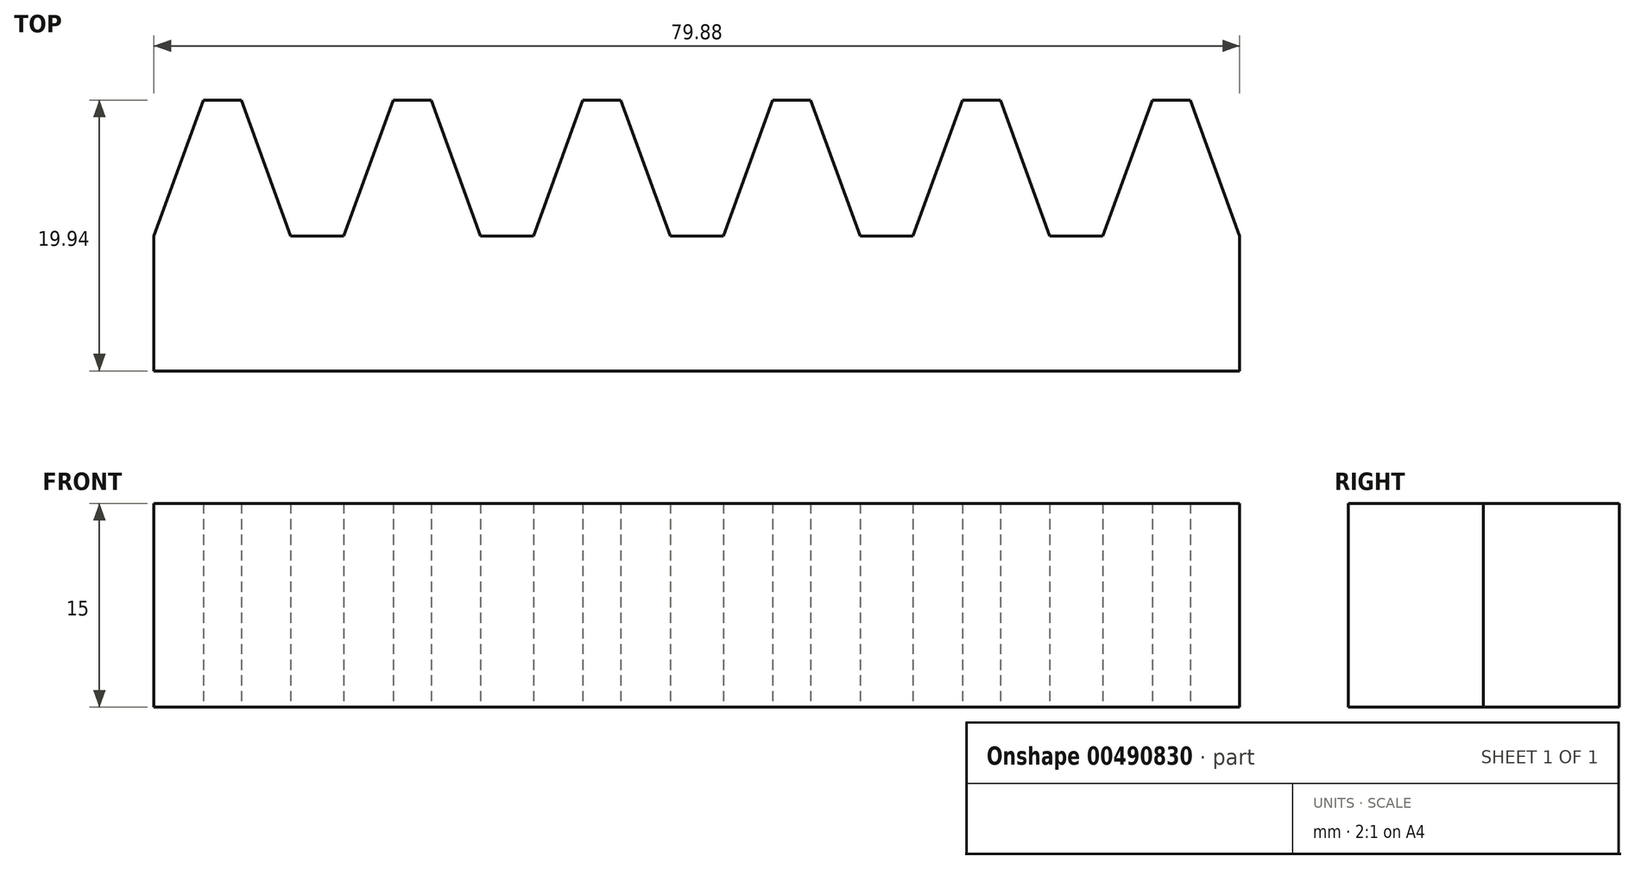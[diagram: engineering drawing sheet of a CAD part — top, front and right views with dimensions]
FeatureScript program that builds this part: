
annotation { "Feature Type Name" : "Feature", "Feature Type Description" : "" }
export const myFeature = defineFeature(function(context is Context, id is Id, definition is map)
    precondition{}
    {
        {
            var Q0;
            Q0=qCreatedBy(makeId("Top.planeOp"),FACE);
            var sketch = newSketch(context, id + "F0", { "sketchPlane" : qUnion([Q0])});
            skPoint(sketch, "E0.middle", {"position": v(1.95, 0.04) * mm});
            skLineSegment(sketch, "E1", {"start": v(1.95, 0.04) * mm, "end": v(5.59, 10.04) * mm});
            skLineSegment(sketch, "E2", {"start": v(5.59, 10.04) * mm, "end": v(8.37, 10.04) * mm});
            skLineSegment(sketch, "E3", {"start": v(8.37, 10.04) * mm, "end": v(12.01, 0.04) * mm});
            skLineSegment(sketch, "E4", {"start": v(12.01, 0.04) * mm, "end": v(15.91, 0.04) * mm});
            skLineSegment(sketch, "E5", {"start": v(15.91, 0.04) * mm, "end": v(19.55, 10.04) * mm});
            skLineSegment(sketch, "E6", {"start": v(19.55, 10.04) * mm, "end": v(22.34, 10.04) * mm});
            skLineSegment(sketch, "E7", {"start": v(22.34, 10.04) * mm, "end": v(25.98, 0.04) * mm});
            skLineSegment(sketch, "E8", {"start": v(25.98, 0.04) * mm, "end": v(29.87, 0.04) * mm});
            skLineSegment(sketch, "E9", {"start": v(29.87, 0.04) * mm, "end": v(33.51, 10.04) * mm});
            skLineSegment(sketch, "E10", {"start": v(33.51, 10.04) * mm, "end": v(36.3, 10.04) * mm});
            skLineSegment(sketch, "E11", {"start": v(36.3, 10.04) * mm, "end": v(39.94, 0.04) * mm});
            skPoint(sketch, "E12.middle", {"position": v(-53.9, 0.04) * mm});
            skLineSegment(sketch, "E13", {"start": v(-39.94, 0.04) * mm, "end": v(-36.3, 10.04) * mm});
            skLineSegment(sketch, "E14", {"start": v(-36.3, 10.04) * mm, "end": v(-33.51, 10.04) * mm});
            skLineSegment(sketch, "E15", {"start": v(-33.51, 10.04) * mm, "end": v(-29.87, 0.04) * mm});
            skLineSegment(sketch, "E16", {"start": v(-29.87, 0.04) * mm, "end": v(-25.97, 0.04) * mm});
            skLineSegment(sketch, "E17", {"start": v(-25.97, 0.04) * mm, "end": v(-22.34, 10.04) * mm});
            skLineSegment(sketch, "E18", {"start": v(-22.34, 10.04) * mm, "end": v(-19.55, 10.04) * mm});
            skLineSegment(sketch, "E19", {"start": v(-19.55, 10.04) * mm, "end": v(-15.91, 0.04) * mm});
            skLineSegment(sketch, "E20", {"start": v(-15.91, 0.04) * mm, "end": v(-12.01, 0.04) * mm});
            skLineSegment(sketch, "E21", {"start": v(-12.01, 0.04) * mm, "end": v(-8.37, 10.04) * mm});
            skLineSegment(sketch, "E22", {"start": v(-8.37, 10.04) * mm, "end": v(-5.59, 10.04) * mm});
            skLineSegment(sketch, "E23", {"start": v(-5.59, 10.04) * mm, "end": v(-1.95, 0.04) * mm});
            skLineSegment(sketch, "E24", {"start": v(-1.95, 0.04) * mm, "end": v(1.95, 0.04) * mm});
            skLineSegment(sketch, "E25", {"start": v(-39.94, -9.9) * mm, "end": v(39.94, -9.9) * mm});
            skPoint(sketch, "E26.orphan", {"position": v(50.26, 10.04) * mm});
            skPoint(sketch, "E27.end.orphan", {"position": v(-50.26, 10.04) * mm});
            skPoint(sketch, "E28.orphan", {"position": v(43.84, 0.04) * mm});
            skPoint(sketch, "E29.end.orphan", {"position": v(-43.84, 0.04) * mm});
            skPoint(sketch, "E30.end.orphan", {"position": v(-47.47, 10.04) * mm});
            skPoint(sketch, "E31.start.orphan", {"position": v(-48.87, 10.04) * mm});
            skLineSegment(sketch, "E32", {"start": v(-39.94, 0.04) * mm, "end": v(-39.94, -9.9) * mm});
            skLineSegment(sketch, "E33", {"start": v(39.94, 0.04) * mm, "end": v(39.94, -9.9) * mm});
            skPoint(sketch, "E34.start.orphan", {"position": v(41.89, 0.04) * mm});
            skPoint(sketch, "E35.start.orphan", {"position": v(-41.89, 0.04) * mm});
            skSolve(sketch);
        }
        {
            var Q0;
            Q0=makeQuery(id+"F0.imprint","IMPRINT",FACE,{"disambiguationData":[TD([[makeQuery(id+"F0.imprint","IMPRINT",EDGE,{"derivedFrom":sQuery(id+"F0.wireOp",EDGE,"E1")}),-1.0]])]});
            extrude(context, id + "F1", {"entities" : qUnion([Q0]), "depth" : 15 * mm});
        }
    });
